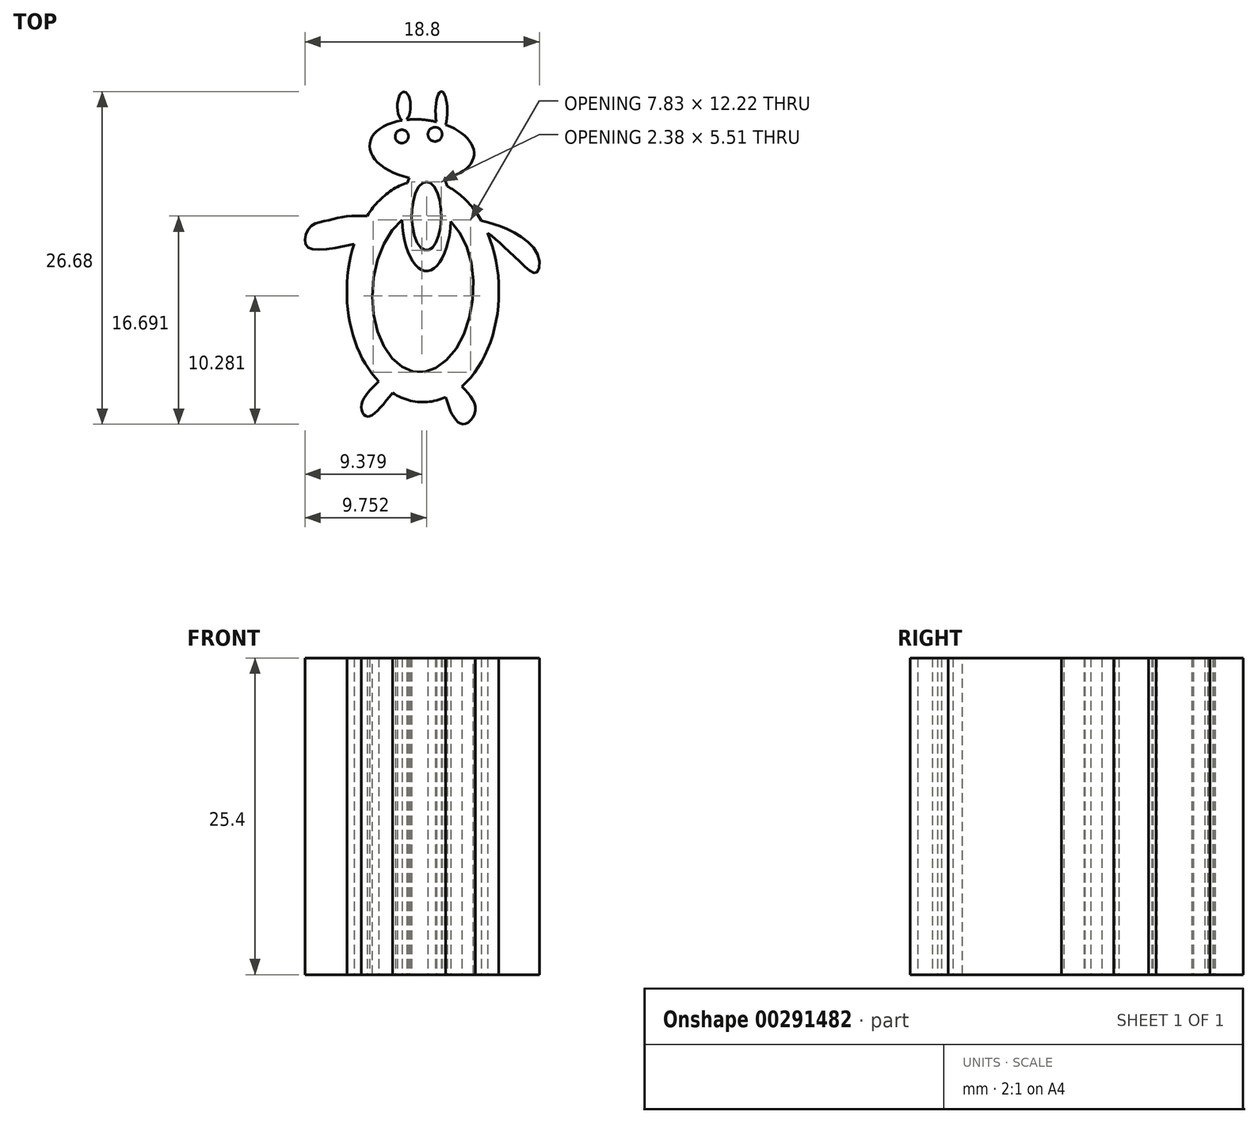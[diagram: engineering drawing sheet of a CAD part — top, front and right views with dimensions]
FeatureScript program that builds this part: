
annotation { "Feature Type Name" : "Feature", "Feature Type Description" : "" }
export const myFeature = defineFeature(function(context is Context, id is Id, definition is map)
    precondition{}
    {
        {
            var Q0;
            Q0=qCreatedBy(makeId("Top.planeOp"),FACE);
            var sketch = newSketch(context, id + "F0", { "sketchPlane" : qUnion([Q0])});
            skEllipticalArc(sketch, "E0", {});
            skEllipticalArc(sketch, "E1", {});
            skEllipticalArc(sketch, "E2", {});
            skPoint(sketch, "E3.0.internal.snap0", {"position": v(-65.84, 43.68) * mm});
            skFitSpline(sketch, "E4", {"points": [v(-66.05, 37.9) * mm, v(-67.85, 37.84) * mm, v(-69.3, 37.52) * mm, v(-70.63, 36.98) * mm, v(-70.9, 35.49) * mm, v(-67.1, 35.66) * mm], "startDerivative": vector(-9.73, 0.26) * mm, "endDerivative": vector(17.84, 4.03) * mm});
            skFitSpline(sketch, "E5", {"points": [v(-56.89, 37.52) * mm, v(-54.8, 36.82) * mm, v(-52.4, 34.84) * mm, v(-52.5, 33.35) * mm, v(-53.62, 34.04) * mm, v(-55.33, 35.66) * mm, v(-56.4, 36.54) * mm], "startDerivative": vector(11.76, -2.76) * mm, "endDerivative": vector(-8, 5.1) * mm});
            skFitSpline(sketch, "E6", {"points": [v(-65.13, 24.62) * mm, v(-66.5, 22.73) * mm, v(-66.04, 21.8) * mm, v(-64.03, 23.7) * mm], "startDerivative": vector(-4.96, -4.81) * mm, "endDerivative": vector(5.46, 6.95) * mm});
            skFitSpline(sketch, "E7", {"points": [v(-59.75, 23.38) * mm, v(-59.09, 21.74) * mm, v(-58.23, 21.2) * mm, v(-57.37, 22.4) * mm, v(-58.45, 24.23) * mm], "startDerivative": vector(1.86, -6.3) * mm, "endDerivative": vector(-5.5, 5.9) * mm});
            skEllipticalArc(sketch, "E8.trimOffspring", {});
            skEllipticalArc(sketch, "E9.trimOffspring", {});
            skEllipticalArc(sketch, "E10.trimOffspring", {});
            skEllipticalArc(sketch, "E11.trimOffspring", {});
            skCircle(sketch, "E12", {"center": v(-63.27, 44.28) * mm, "radius": 0.53 * mm});
            skCircle(sketch, "E13", {"center": v(-60.61, 44.45) * mm, "radius": 0.57 * mm});
            skEllipticalArc(sketch, "E14", {});
            skEllipticalArc(sketch, "E15.trimOffspring", {});
            skEllipticalArc(sketch, "E16.trimOffspring", {});
            skFitSpline(sketch, "E17", {"points": [v(-60.15, 45.38) * mm, v(-60.15, 45.38) * mm], "startDerivative": vector(0, 0) * mm, "endDerivative": vector(0, 0) * mm});
            skEllipticalArc(sketch, "E18", {});
            skEllipticalArc(sketch, "E19.trimOffspring", {});
            skEllipse(sketch, "E20", {"center": v(-61.29, 37.9) * mm, "majorRadius": 2.76 * mm, "minorRadius": 1.19 * mm, "majorAxis": v(0, 1)});
            skEllipticalArc(sketch, "E21", {});
            skFitSpline(sketch, "E22", {"points": [v(-62.7, 40.96) * mm, v(-62.85, 40.55) * mm], "startDerivative": vector(-0.16, -0.41) * mm, "endDerivative": vector(-0.16, -0.41) * mm});
            skFitSpline(sketch, "E23", {"points": [v(-59.86, 40.91) * mm, v(-59.64, 40.28) * mm], "startDerivative": vector(0.22, -0.63) * mm, "endDerivative": vector(0.22, -0.63) * mm});
            const initialGuessF0  = {"E0": [-0.06166298944709939, 0.04322030442921584, 0.9939354249439386, -0.1099653174483315, 0.004202239200969528, 0.0023985058559930867, 5.219701271541227, 1.157997573679443], "E1": [-0.06309740005149882, 0.04668027723545083, 0, -1, 0.0011745699840170429, 0.0005321858043973299, 0.43630267831540737, 5.965538311036555], "E2": [-0.061584607914449176, 0.03185421882332729, 0, 1, 0.008890226487152977, 0.0060959567290454555, 0.20870078019734273, 0.8227075011066192], "E8.trimOffspring": [-0.061584607914449176, 0.03185421882332729, 0, 1, 0.008890226487152977, 0.0060959567290454555, 1.1281081533731059, 2.5218725830319184], "E9.trimOffspring": [-0.061584607914449176, 0.03185421882332729, 0, 1, 0.008890226487152977, 0.0060959567290454555, 5.403295472669219, 5.9593109812287794], "E10.trimOffspring": [-0.061584607914449176, 0.03185421882332729, 0, 1, 0.008890226487152977, 0.0060959567290454555, 2.7294760898800297, 3.4469443949982725], "E11.trimOffspring": [-0.061584607914449176, 0.03185421882332729, 0, 1, 0.008890226487152977, 0.0060959567290454555, 3.68161117012392, 5.268027114324978], "E14": [-0.061288103461265564, 0.03789125755429268, 0, 1, 0.004402123391628265, 0.001957366463477211, 0.9218879607459195, 5.2865644403830645], "E15.trimOffspring": [-0.061288103461265564, 0.03789125755429268, 0, 1, 0.004402123391628265, 0.001957366463477211, 5.468672063144031, 0.7987989165485802], "E16.trimOffspring": [-0.06166298944709939, 0.04322030442921584, 0.9939354249439386, -0.1099653174483315, 0.004202239200969528, 0.0023985058559930867, 2.026319102122986, 4.527376044557136], "E18": [-0.060097575187683105, 0.046286147087812424, 0, 1, 0.0015987232327461243, 0.00047258071452850516, 3.9812346301084753, 2.1231153153792675], "E19.trimOffspring": [-0.06166298944709939, 0.04322030442921584, 0.9939354249439386, -0.1099653174483315, 0.004202239200969528, 0.0023985058559930867, 1.3522357029318564, 1.9270491674836365], "E21": [-0.061584607914449176, 0.03185421882332729, 0.06466533548688842, 0.9979070068830904, 0.00649183457784156, 0.004037593494413293, 0.5250266047593702, 5.799663575949532]};
            skSetInitialGuess(sketch, initialGuessF0);
            skSolve(sketch);
        }
        {
            var Q0;
            Q0 = qSketchRegion(id + "F0", true);
            extrude(context, id + "F1", {"entities" : qUnion([Q0]), "depth" : 25.4 * mm});
        }
    });
